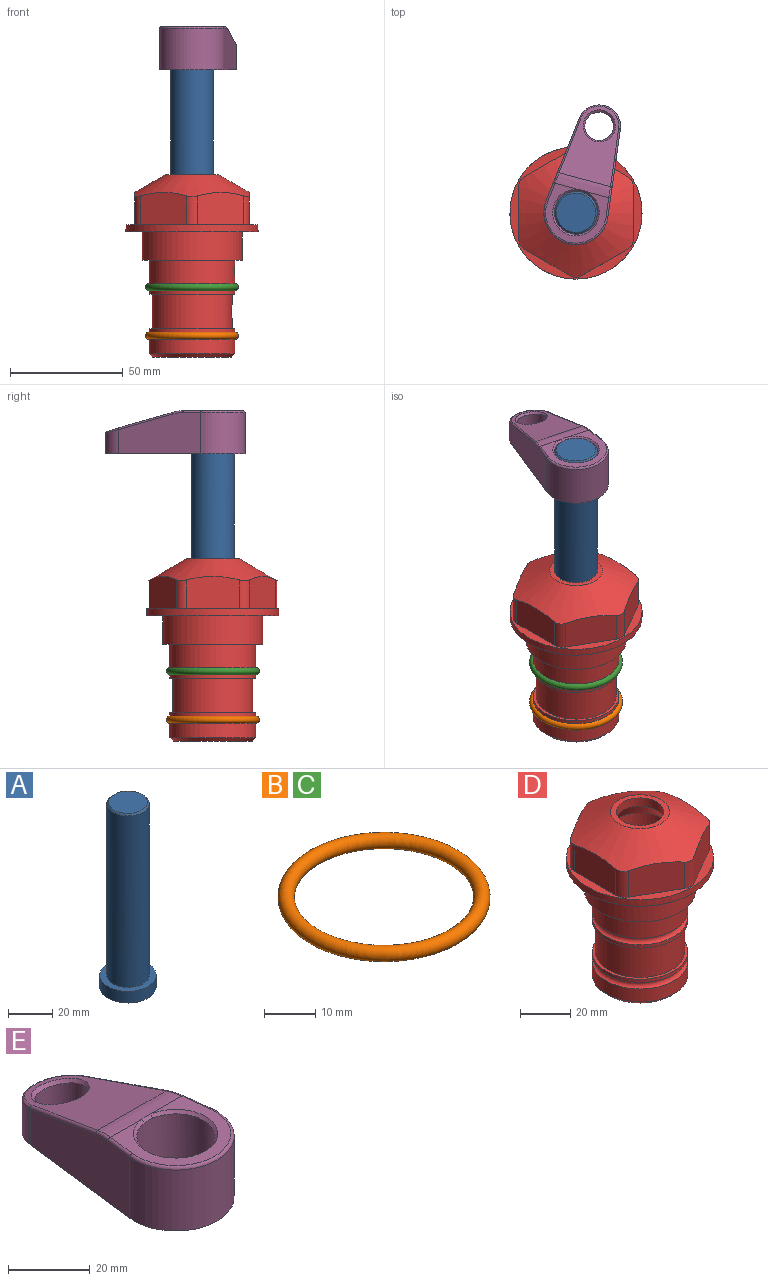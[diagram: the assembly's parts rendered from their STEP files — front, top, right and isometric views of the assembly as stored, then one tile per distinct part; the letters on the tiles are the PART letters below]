
ASSEMBLY  parts=5 mates=4
PART A: 6 faces, bbox 25.4x25.4x101.6 mm
  f0: plane 17.46x17.46mm, normal (0,0,1), area 239.5mm2, adj f5
  f1: plane 25.4x25.4mm, normal (0,0,-1), area 506.7mm2, adj f2
  f2: cylinder r=12.7mm len=25.4mm, axis (0,0,1), area 506.7mm2, adj f1,f3
  f3: plane 25.4x25.4mm, normal (0,0,1), area 221.7mm2, adj f2,f4
  f4: cylinder r=9.53mm len=94.46mm, axis (0,0,1), area 5653mm2, adj f3,f5
  f5: cone r=8.73mm half-angle=45deg, axis (0,0,-1), area 64.4mm2, adj f0,f4
PART B: 1 faces, bbox 44.7x44.7x3.2 mm
  f0: torus R=19.05mm, axis (0,0,1), area 1193.9mm2
PART C: same geometry as B
PART D: 36 faces, bbox 58.7x58.7x81 mm
  f0: cylinder r=17.78mm len=35.56mm, axis (0,0,1), area 1670.8mm2, adj f23,f24,f31
  f1: cylinder r=19.05mm len=38.1mm, axis (0,0,1), area 1191.9mm2, adj f26,f27,f30
  f2: plane 58.66x58.66mm, normal (0,0,-1), area 1150.6mm2, adj f3,f28
  f3: cylinder r=29.33mm len=58.66mm, axis (0,0,-1), area 585.1mm2, adj f2,f4
  f4: plane 58.66x58.66mm, normal (0,0,1), area 475.9mm2, adj f3,f5,f6,f7,f8,f9,f10,f11
  f5: plane 20.32x14.34mm, normal (-0.5,0.87,0), area 324.4mm2, adj f4,f15,f16,f17
  f6: plane 20.32x14.34mm, normal (0.5,0.87,0), area 324.4mm2, adj f4,f14,f15,f17
  f7: plane 23.48x14.34mm, normal (1,0,0), area 324.4mm2, adj f4,f13,f14,f17
  f8: plane 20.32x14.34mm, normal (0.5,-0.87,0), area 324.4mm2, adj f4,f12,f13,f17
  f9: plane 20.32x14.34mm, normal (-0.5,-0.87,0), area 324.4mm2, adj f4,f11,f12,f17
  f10: plane 23.48x14.34mm, normal (-1,0,0), area 324.4mm2, adj f4,f11,f16,f17
  f11: cylinder r=5.08mm len=12.85mm, axis (0,0,-1), area 67.2mm2, adj f4,f9,f10,f17
  f12: cylinder r=5.08mm len=12.85mm, axis (0,0,-1), area 67.2mm2, adj f4,f8,f9,f17
  f13: cylinder r=5.08mm len=12.85mm, axis (0,0,-1), area 67.2mm2, adj f4,f7,f8,f17
  f14: cylinder r=5.08mm len=12.85mm, axis (0,0,-1), area 67.2mm2, adj f4,f6,f7,f17
  f15: cylinder r=5.08mm len=12.85mm, axis (0,0,-1), area 67.2mm2, adj f4,f5,f6,f17
  f16: cylinder r=5.08mm len=12.85mm, axis (0,0,-1), area 67.2mm2, adj f4,f5,f10,f17
  f17: cone r=11.73mm half-angle=60deg, axis (0,0,-1), area 2071.8mm2, adj f5,f6,f7,f8,f9,f10,f11,f12
  f18: plane 23.46x23.46mm, normal (0,0,1), area 147.4mm2, adj f17,f35
  f19: plane 34.93x34.93mm, normal (0,0,-1), area 958mm2, adj f29
  f20: cylinder r=19.05mm len=38.1mm, axis (0,0,1), area 760.1mm2, adj f21,f29
  f21: torus R=19.05mm, axis (0,0,1), area 565.3mm2, adj f20,f22
  f22: cylinder r=19.05mm len=38.1mm, axis (0,0,1), area 190mm2, adj f21,f23
  f23: plane 38.1x38.1mm, normal (0,0,1), area 146.9mm2, adj f0,f22
  f24: plane 38.1x38.1mm, normal (0,0,-1), area 146.9mm2, adj f0,f25
  f25: cylinder r=19.05mm len=38.1mm, axis (0,0,1), area 190mm2, adj f24,f26
  f26: torus R=19.05mm, axis (0,0,1), area 565.3mm2, adj f1,f25
  f27: plane 44.45x44.45mm, normal (0,0,-1), area 411.7mm2, adj f1,f28
  f28: cylinder r=22.23mm len=44.45mm, axis (0,0,1), area 1773.5mm2, adj f2,f27
  f29: cone r=19.05mm half-angle=45deg, axis (0,0,1), area 257.5mm2, adj f19,f20
  f30: cylinder r=3.17mm len=6.75mm, axis (-1,0,0), area 128mm2, adj f1,f33
  f31: cylinder r=3.17mm len=6.35mm, axis (-1,0,0), area 102.5mm2, adj f0,f33
  f32: plane 25.4x25.4mm, normal (0,0,1), area 506.7mm2, adj f33
  f33: cylinder r=12.7mm len=66.42mm, axis (0,0,-1), area 5236.2mm2, adj f30,f31,f32,f34
  f34: cone r=9.53mm half-angle=30deg, axis (0,0,-1), area 443.4mm2, adj f33,f35
  f35: cylinder r=9.53mm len=19.05mm, axis (0,0,-1), area 240.9mm2, adj f18,f34
PART E: 31 faces, bbox 31.7x65.5x19.8 mm
  f0: plane 39.12x18.26mm, normal (0.99,0.12,0), area 612.2mm2, adj f1,f4,f7,f11,f13,f15
  f1: cylinder r=9.53mm len=18.91mm, axis (0,0,-1), area 296.1mm2, adj f0,f2,f7,f17
  f2: plane 39.12x18.26mm, normal (-0.99,0.12,0), area 612.2mm2, adj f1,f4,f7,f12,f14,f16
  f3: cylinder r=6.35mm len=12.7mm, axis (0,0,-1), area 362.4mm2, adj f7,f18
  f4: cylinder r=14.29mm len=28.58mm, axis (0,0,-1), area 882.2mm2, adj f0,f2,f7,f10
  f5: cylinder r=9.53mm len=19.05mm, axis (0,0,-1), area 1092.6mm2, adj f7,f19,f20
  f6: plane 26.99x23.69mm, normal (0,0,1), area 216.2mm2, adj f9,f10,f11,f12,f19
  f7: plane 63.5x28.58mm, normal (0,0,-1), area 661.8mm2, adj f0,f1,f2,f3,f4,f5,f22,f23
  f8: plane 33.52x23.6mm, normal (0,0.26,0.97), area 486mm2, adj f9,f15,f16,f17,f18
  f9: cylinder r=19.05mm len=24.72mm, axis (1,0,0), area 120.4mm2, adj f6,f8,f13,f14,f20
  f10: torus R=13.49mm, axis (0,0,1), area 59mm2, adj f4,f6,f11,f12
  f11: cylinder r=0.79mm len=8.67mm, axis (0.12,-0.99,0), area 10.8mm2, adj f0,f6,f10,f13
  f12: cylinder r=0.79mm len=8.67mm, axis (0.12,0.99,0), area 10.8mm2, adj f2,f6,f10,f14
  f13: bspline ~4.95x1.42mm, area 6.1mm2, adj f0,f9,f11,f15
  f14: bspline ~4.95x1.42mm, area 6.1mm2, adj f2,f9,f12,f16
  f15: cylinder r=0.79mm len=25.95mm, axis (0.12,-0.96,0.26), area 32.9mm2, adj f0,f8,f13,f17
  f16: cylinder r=0.79mm len=25.95mm, axis (0.12,0.96,-0.26), area 32.9mm2, adj f2,f8,f14,f17
  f17: bspline ~18.91x8.38mm, area 30mm2, adj f1,f8,f15,f16
  f18: bspline ~14.29x14.29mm, area 48.3mm2, adj f3,f8
  f19: cone r=9.53mm half-angle=45deg, axis (0,0,1), area 66.5mm2, adj f5,f6,f20
  f20: bspline ~3.22x0.96mm, area 3.5mm2, adj f5,f9,f19
  f21: plane 2.75x2.72mm, normal (0,0,-1), area 2.9mm2, adj f23,f25,f28
  f22: plane 23.05x15.88mm, normal (-0.99,-0.12,0), area 323.6mm2, adj f7,f25,f26,f27,f28,f29
  f23: plane 23.05x15.88mm, normal (0.99,-0.12,0), area 323.6mm2, adj f7,f21,f25,f27,f28,f30
  f24: cylinder r=9.53mm len=10.69mm, axis (0,0,-1), area 114.7mm2, adj f7,f27,f29,f30
  f25: cylinder r=12.7mm len=20.59mm, axis (0,0,-1), area 381.1mm2, adj f7,f21,f22,f23,f26,f28
  f26: plane 2.75x2.72mm, normal (0,0,-1), area 2.9mm2, adj f22,f25,f28
  f27: plane 19.72x18.37mm, normal (0,-0.26,-0.97), area 291.8mm2, adj f22,f23,f24,f28,f29,f30
  f28: cylinder r=15.88mm len=19.92mm, axis (1,0,0), area 54.8mm2, adj f21,f22,f23,f25,f26,f27
  f29: cylinder r=1.59mm len=11mm, axis (0,0,-1), area 34.7mm2, adj f7,f22,f24,f27
  f30: cylinder r=1.59mm len=11mm, axis (0,0,-1), area 34.7mm2, adj f7,f23,f24,f27
PLACE A rot(axis=(0,0,-1),15deg) t=(0,0,27.55)mm
PLACE B t=(0,0,-21.59)mm
PLACE C at identity
PLACE D at identity fixed
PLACE E rot(axis=(0,0,-1),15deg) t=(0,0,27.55)mm
MATE fastened A.f2 <-> E.f4  axis (0,0,1) through (0,0,91.05)mm
MATE fastened C.f0 <-> D.f0  axis (0,0,1) through (0,0,-24.51)mm
MATE cylindrical A.f2 <-> D.f0  axis (0,0,-1) through (0,0,-10.55)mm
MATE fastened D.f0 <-> B.f0  axis (0,0,1) through (0,0,-46.1)mm
